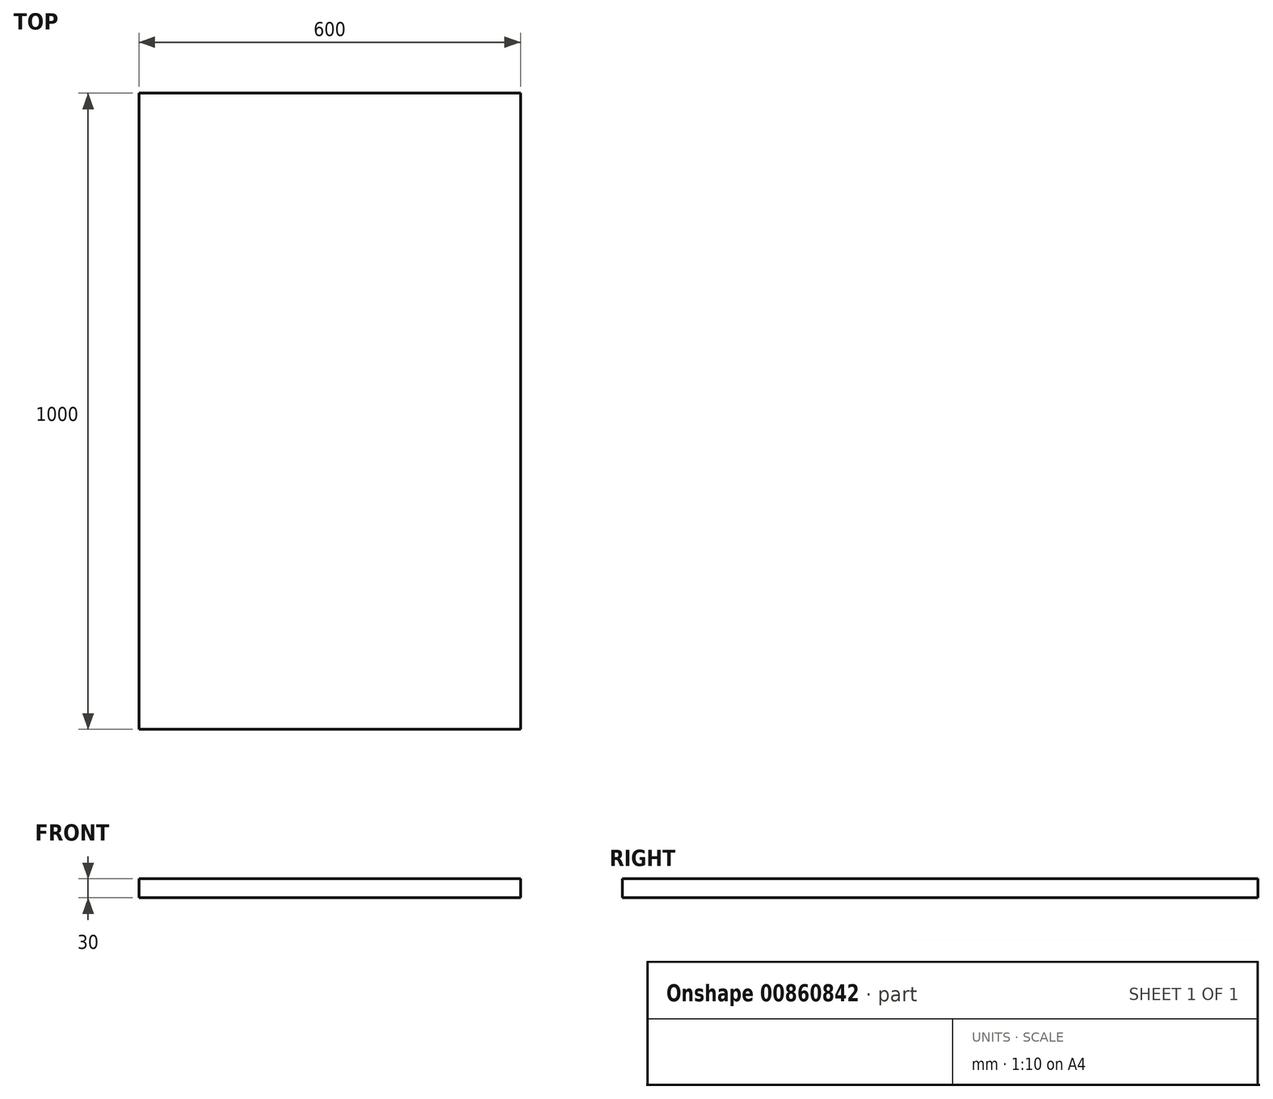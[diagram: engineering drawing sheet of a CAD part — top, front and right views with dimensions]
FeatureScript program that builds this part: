
annotation { "Feature Type Name" : "Feature", "Feature Type Description" : "" }
export const myFeature = defineFeature(function(context is Context, id is Id, definition is map)
    precondition{}
    {
        {
            var Q0;
            Q0=qCreatedBy(makeId("Top.planeOp"),FACE);
            var sketch = newSketch(context, id + "F0", { "sketchPlane" : qUnion([Q0])});
            skLineSegment(sketch, "E0.bottom", {"start": v(-54.49, 953.6) * mm, "end": v(545.51, 953.6) * mm});
            skLineSegment(sketch, "E0.top", {"start": v(-54.49, -46.4) * mm, "end": v(545.51, -46.4) * mm});
            skLineSegment(sketch, "E0.left", {"start": v(-54.49, 953.6) * mm, "end": v(-54.49, -46.4) * mm});
            skLineSegment(sketch, "E0.right", {"start": v(545.51, 953.6) * mm, "end": v(545.51, -46.4) * mm});
            skSolve(sketch);
        }
        {
            var Q0;
            Q0=makeQuery(id+"F0.imprint","IMPRINT",FACE,{"disambiguationData":[TD([[makeQuery(id+"F0.imprint","IMPRINT",EDGE,{"derivedFrom":sQuery(id+"F0.wireOp",EDGE,"E0.bottom")}),-1.0]])]});
            extrude(context, id + "F1", {"entities" : qUnion([Q0]), "depth" : 30 * mm, "offsetDistance" : 25 * mm});
        }
    });
